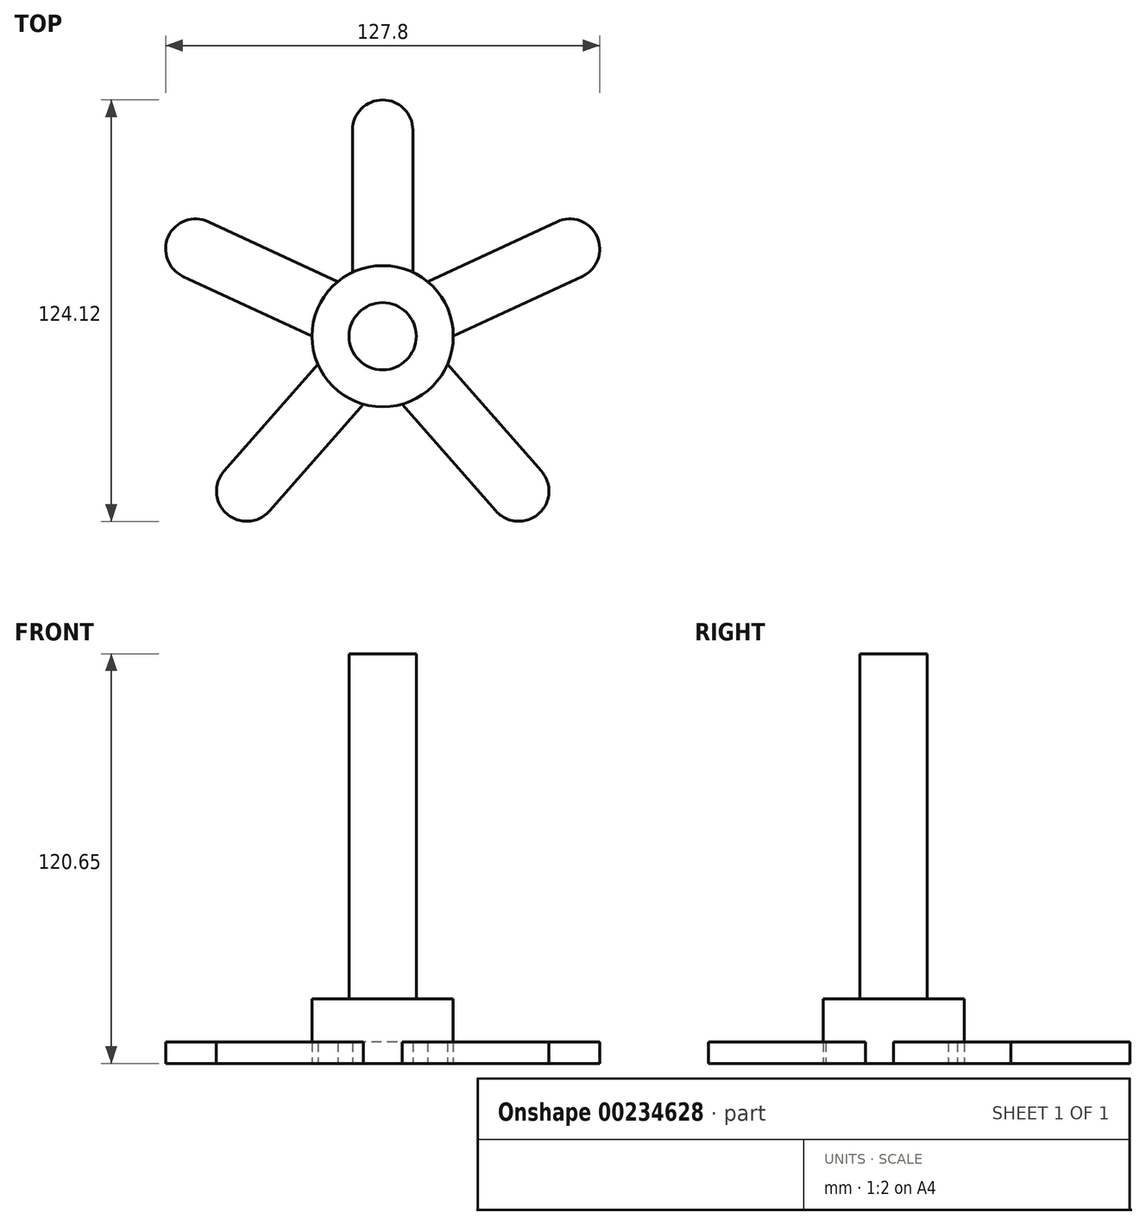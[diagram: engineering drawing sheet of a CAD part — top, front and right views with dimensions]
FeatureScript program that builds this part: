
annotation { "Feature Type Name" : "Feature", "Feature Type Description" : "" }
export const myFeature = defineFeature(function(context is Context, id is Id, definition is map)
    precondition{}
    {
        {
            var Q0;
            Q0=qCreatedBy(makeId("Top.planeOp"),FACE);
            var sketch = newSketch(context, id + "F0", { "sketchPlane" : qUnion([Q0])});
            skCircle(sketch, "E0", {"center": v(0, 0) * mm, "radius": 20.8 * mm});
            skLineSegment(sketch, "E1", {"start": v(-8.9, 18.8) * mm, "end": v(-8.9, 60.7) * mm});
            skArc(sketch, "E2", {"start": v(0, 69.6) * mm, "mid": v(-6.29, 67) * mm, "end": v(-8.9, 60.7) * mm});
            skArc(sketch, "E3", {"start": v(-51.27, 33.73) * mm, "mid": v(-63.08, 29.4) * mm, "end": v(-58.75, 17.6) * mm});
            skLineSegment(sketch, "E4", {"start": v(-19.08, -8.26) * mm, "end": v(-46.73, -39.76) * mm});
            skArc(sketch, "E5", {"start": v(-46.73, -39.76) * mm, "mid": v(-45.88, -52.34) * mm, "end": v(-33.3, -51.42) * mm});
            skLineSegment(sketch, "E6", {"start": v(-33.3, -51.42) * mm, "end": v(-5.72, -20) * mm});
            skLineSegment(sketch, "E7", {"start": v(-51.27, 33.73) * mm, "end": v(-13.19, 16.07) * mm});
            skLineSegment(sketch, "E8", {"start": v(-58.75, 17.6) * mm, "end": v(-20.8, 0) * mm});
            skArc(sketch, "E9.MirrorCS", {"start": v(0, 69.6) * mm, "mid": v(6.29, 67) * mm, "end": v(8.9, 60.7) * mm});
            skLineSegment(sketch, "E10.MirrorCS", {"start": v(8.9, 18.8) * mm, "end": v(8.9, 60.7) * mm});
            skLineSegment(sketch, "E11.MirrorCS", {"start": v(51.27, 33.73) * mm, "end": v(13.19, 16.07) * mm});
            skArc(sketch, "E12.MirrorCS", {"start": v(51.27, 33.73) * mm, "mid": v(63.08, 29.4) * mm, "end": v(58.75, 17.6) * mm});
            skLineSegment(sketch, "E13.MirrorCS", {"start": v(58.75, 17.6) * mm, "end": v(20.8, 0) * mm});
            skLineSegment(sketch, "E14.MirrorCS", {"start": v(19.08, -8.26) * mm, "end": v(46.73, -39.76) * mm});
            skArc(sketch, "E15.MirrorCS", {"start": v(46.73, -39.76) * mm, "mid": v(45.88, -52.34) * mm, "end": v(33.3, -51.42) * mm});
            skLineSegment(sketch, "E16.MirrorCS", {"start": v(33.3, -51.42) * mm, "end": v(5.72, -20) * mm});
            skSolve(sketch);
        }
        {
            var Q0;
            Q0=makeQuery(id+"F0.imprint","IMPRINT",FACE,{"disambiguationData":[TD([[makeQuery(id+"F0.imprint","IMPRINT",EDGE,{"derivedFrom":sQuery(id+"F0.wireOp",EDGE,"E3")}),1.0]])]});
            var Q1;
            {var subQ0=sQuery(id+"F0.wireOp",EDGE,"E1");Q1=makeQuery(id+"F0.imprint","IMPRINT",FACE,{"disambiguationData":[TD([[makeQuery(id+"F0.imprint","IMPRINT",EDGE,{"derivedFrom":subQ0}),-1.0]])]});}
            var Q2;
            {var subQ0=sQuery(id+"F0.wireOp",EDGE,"E11.MirrorCS");Q2=makeQuery(id+"F0.imprint","IMPRINT",FACE,{"disambiguationData":[TD([[makeQuery(id+"F0.imprint","IMPRINT",EDGE,{"derivedFrom":subQ0}),1.0]])]});}
            var Q3;
            {var subQ0=sQuery(id+"F0.wireOp",EDGE,"E14.MirrorCS");Q3=makeQuery(id+"F0.imprint","IMPRINT",FACE,{"disambiguationData":[TD([[makeQuery(id+"F0.imprint","IMPRINT",EDGE,{"derivedFrom":subQ0}),-1.0]])]});}
            var Q4;
            {var subQ0=sQuery(id+"F0.wireOp",EDGE,"E4");Q4=makeQuery(id+"F0.imprint","IMPRINT",FACE,{"disambiguationData":[TD([[makeQuery(id+"F0.imprint","IMPRINT",EDGE,{"derivedFrom":subQ0}),1.0]])]});}
            extrude(context, id + "F1", {"entities" : qUnion([Q0, Q1, Q2, Q3, Q4]), "depth" : 6.35 * mm});
        }
        {
            var Q0;
            {var subQ0=sQuery(id+"F0.wireOp",EDGE,"E0");var subQ6=makeQuery(id+"F0.imprint","INTERSECT",VERTEX,{"derivedFrom":[subQ0,sQuery(id+"F0.wireOp",EDGE,"E11.MirrorCS")]});Q0=makeQuery(id+"F0.imprint","IMPRINT",FACE,{"disambiguationData":[TD([[makeQuery(id+"F0.imprint","IMPRINT",EDGE,{"disambiguationData":[TD([[subQ6,1.0]])],"derivedFrom":subQ0}),1.0]])]});}
            extrude(context, id + "F2", {"entities" : qUnion([Q0]), "depth" : 19.05 * mm});
        }
        {
            var Q0;
            Q0=makeQuery(id+"F2.opExtrude","CAP_FACE",FACE,{"disambiguationData":[OSD([sQuery(id+"F0.wireOp",EDGE,"E0")])],"isStart":false});
            var sketch = newSketch(context, id + "F3", { "sketchPlane" : qUnion([Q0])});
            skCircle(sketch, "E17", {"center": v(0, 0) * mm, "radius": 9.9 * mm});
            skSolve(sketch);
        }
        {
            var Q0;
            Q0 = qSketchRegion(id + "F3", true);
            extrude(context, id + "F4", {"entities" : qUnion([Q0]), "operationType" : NewBodyOperationType.ADD, "depth" : 101.6 * mm});
        }
    });
